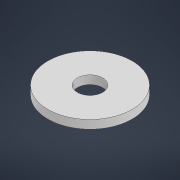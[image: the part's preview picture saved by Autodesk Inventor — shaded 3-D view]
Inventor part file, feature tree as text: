
AUTODESK INVENTOR PART (.ipt)
format: ipt  version: 2022 (Build 260153000, 153)  size: 92,160 bytes
history: native  units: mm
features: other x1, extrude x1, sketch x1
ambient origin geometry x8: Origin, YZ Plane, XZ Plane, XY Plane, X Axis, Y Axis, Z Axis, Center Point
bodies: Body1 (feature_tree)
feature tree (3):
  other  "Sólido1"
  extrude  "Extrusão1"  Depth=10.0mm
  sketch  "Esboço1"  dims[d0=100.0mm d1=30.0mm d2=10.0mm d3=0.0mm]
